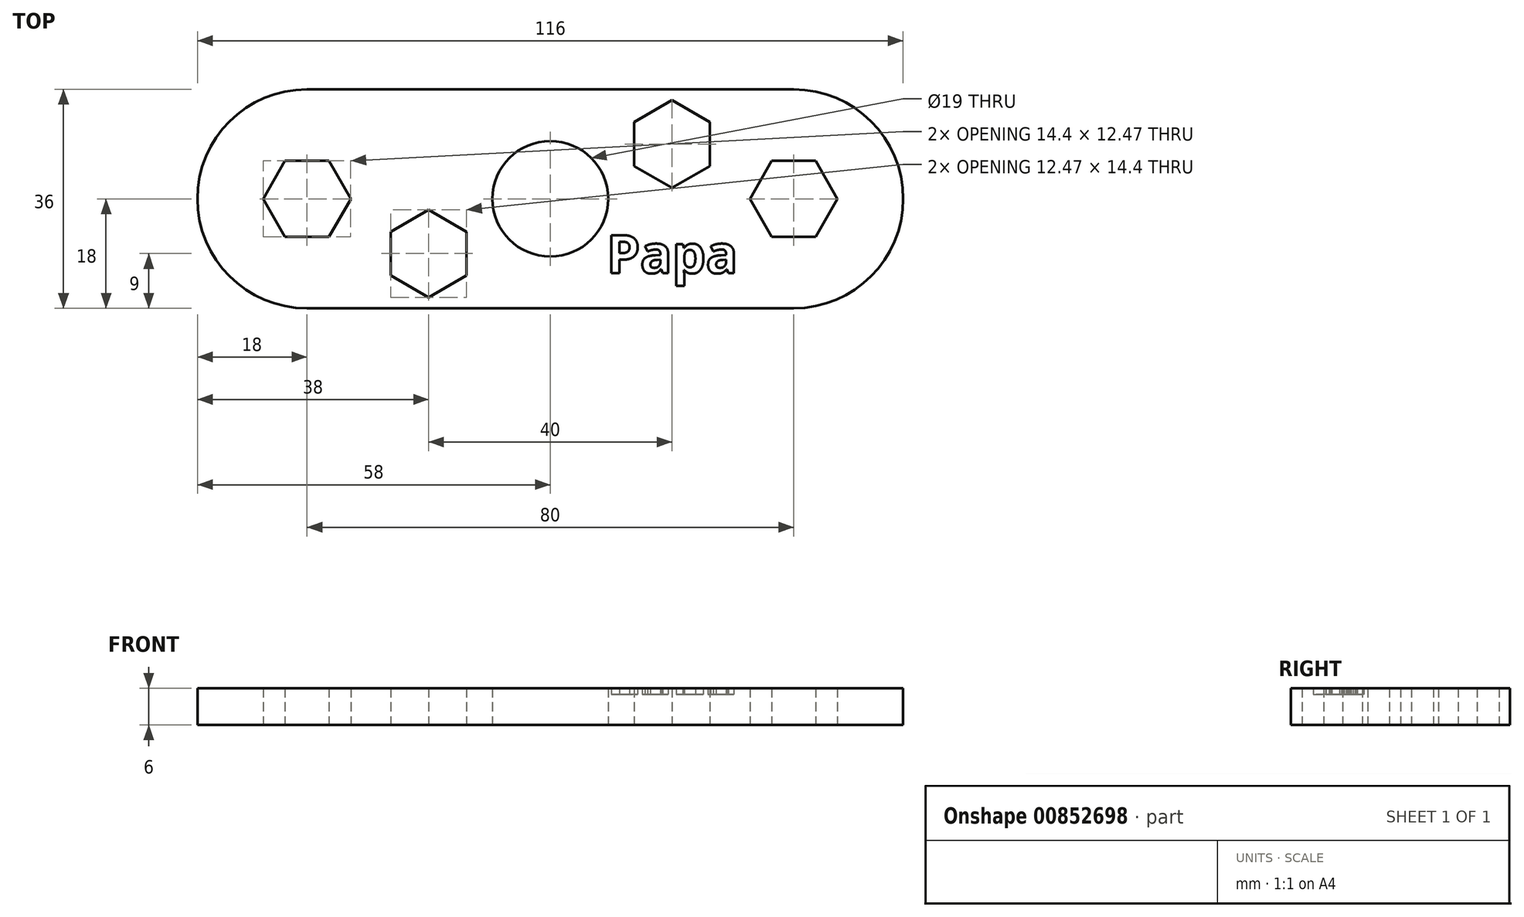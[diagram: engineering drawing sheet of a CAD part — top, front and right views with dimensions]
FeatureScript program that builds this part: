
annotation { "Feature Type Name" : "Feature", "Feature Type Description" : "" }
export const myFeature = defineFeature(function(context is Context, id is Id, definition is map)
    precondition{}
    {
        {
            var Q0;
            Q0=qCreatedBy(makeId("Top.planeOp"),FACE);
            var sketch = newSketch(context, id + "F0", { "sketchPlane" : qUnion([Q0])});
            skPoint(sketch, "E0.middle", {"position": v(0, 0) * mm});
            skCircle(sketch, "E1", {"center": v(0, 0) * mm, "radius": 9.5 * mm});
            skCircle(sketch, "E2.cCircle", {"center": v(40, 0) * mm, "radius": 7.2 * mm, "construction": true});
            skLineSegment(sketch, "E2.0", {"start": v(47.2, 0) * mm, "end": v(43.6, -6.24) * mm});
            skLineSegment(sketch, "E2.1", {"start": v(43.6, -6.24) * mm, "end": v(36.4, -6.24) * mm});
            skLineSegment(sketch, "E2.2", {"start": v(36.4, -6.24) * mm, "end": v(32.8, 0) * mm});
            skLineSegment(sketch, "E2.3", {"start": v(32.8, 0) * mm, "end": v(36.4, 6.24) * mm});
            skLineSegment(sketch, "E2.4", {"start": v(36.4, 6.24) * mm, "end": v(43.6, 6.24) * mm});
            skLineSegment(sketch, "E2.5", {"start": v(43.6, 6.24) * mm, "end": v(47.2, 0) * mm});
            skPoint(sketch, "E3", {"position": v(20, 0) * mm});
            skText(sketch, "E4", { "text": "Papa", "fontName": "OpenSans-Bold.ttf"});
            skLineSegment(sketch, "E5.top", {"start": v(0, 18) * mm, "end": v(40, 18) * mm});
            skLineSegment(sketch, "E6.top", {"start": v(40, 10) * mm, "end": v(40, 10) * mm});
            skLineSegment(sketch, "E7.top", {"start": v(0, 18) * mm, "end": v(-40, 18) * mm});
            skLineSegment(sketch, "E7.left", {"start": v(0, 0) * mm, "end": v(0, 18) * mm});
            skLineSegment(sketch, "E8.top", {"start": v(0, -18) * mm, "end": v(-40, -18) * mm});
            skLineSegment(sketch, "E8.left", {"start": v(0, 0) * mm, "end": v(0, -18) * mm});
            skLineSegment(sketch, "E9.top", {"start": v(0, -18) * mm, "end": v(40, -18) * mm});
            skArc(sketch, "E10", {"start": v(40, -18) * mm, "mid": v(58, 0) * mm, "end": v(40, 18) * mm});
            skArc(sketch, "E11", {"start": v(-40, 18) * mm, "mid": v(-58, 0) * mm, "end": v(-40, -18) * mm});
            skPoint(sketch, "E12", {"position": v(-20, -9) * mm});
            skCircle(sketch, "E13.cCircle", {"center": v(-20, -9) * mm, "radius": 7.2 * mm, "construction": true});
            skLineSegment(sketch, "E13.0", {"start": v(-20, -1.8) * mm, "end": v(-13.76, -5.4) * mm});
            skLineSegment(sketch, "E13.1", {"start": v(-13.76, -5.4) * mm, "end": v(-13.76, -12.6) * mm});
            skLineSegment(sketch, "E13.2", {"start": v(-13.76, -12.6) * mm, "end": v(-20, -16.2) * mm});
            skLineSegment(sketch, "E13.3", {"start": v(-20, -16.2) * mm, "end": v(-26.24, -12.6) * mm});
            skLineSegment(sketch, "E13.4", {"start": v(-26.24, -12.6) * mm, "end": v(-26.24, -5.4) * mm});
            skLineSegment(sketch, "E13.5", {"start": v(-26.24, -5.4) * mm, "end": v(-20, -1.8) * mm});
            skCircle(sketch, "E14.cCircle", {"center": v(-40, 0) * mm, "radius": 7.2 * mm, "construction": true});
            skLineSegment(sketch, "E14.0", {"start": v(-32.8, 0) * mm, "end": v(-36.4, -6.24) * mm});
            skLineSegment(sketch, "E14.1", {"start": v(-36.4, -6.24) * mm, "end": v(-43.6, -6.24) * mm});
            skLineSegment(sketch, "E14.2", {"start": v(-43.6, -6.24) * mm, "end": v(-47.2, 0) * mm});
            skLineSegment(sketch, "E14.3", {"start": v(-47.2, 0) * mm, "end": v(-43.6, 6.24) * mm});
            skLineSegment(sketch, "E14.4", {"start": v(-43.6, 6.24) * mm, "end": v(-36.4, 6.24) * mm});
            skLineSegment(sketch, "E14.5", {"start": v(-36.4, 6.24) * mm, "end": v(-32.8, 0) * mm});
            skPoint(sketch, "E15", {"position": v(20, 9) * mm});
            skCircle(sketch, "E16.cCircle", {"center": v(20, 9) * mm, "radius": 7.2 * mm, "construction": true});
            skLineSegment(sketch, "E16.0", {"start": v(20, 16.2) * mm, "end": v(26.24, 12.6) * mm});
            skLineSegment(sketch, "E16.1", {"start": v(26.24, 12.6) * mm, "end": v(26.24, 5.4) * mm});
            skLineSegment(sketch, "E16.2", {"start": v(26.24, 5.4) * mm, "end": v(20, 1.8) * mm});
            skLineSegment(sketch, "E16.3", {"start": v(20, 1.8) * mm, "end": v(13.76, 5.4) * mm});
            skLineSegment(sketch, "E16.4", {"start": v(13.76, 5.4) * mm, "end": v(13.76, 12.6) * mm});
            skLineSegment(sketch, "E16.5", {"start": v(13.76, 12.6) * mm, "end": v(20, 16.2) * mm});
            const initialGuessF0  = {"E4": [0.00927, -0.01223, 1, 0, 0.00629]};
            skSetInitialGuess(sketch, initialGuessF0);
            skSolve(sketch);
        }
        {
            var Q0;
            Q0 = qSketchRegion(id + "F0", true);
            extrude(context, id + "F1", {"entities" : qUnion([Q0]), "depth" : 6 * mm, "offsetDistance" : 25 * mm});
        }
        {
            var Q0;
            Q0=makeQuery(id+"F0.imprint","IMPRINT",FACE,{"disambiguationData":[TD([[makeQuery(id+"F0.imprint","IMPRINT",EDGE,{"derivedFrom":sQuery(id+"F0.wireOp",EDGE,"E4.sketch_text.stroke-0")}),-1.0]])]});
            var Q1;
            Q1=makeQuery(id+"F0.imprint","IMPRINT",FACE,{"disambiguationData":[TD([[makeQuery(id+"F0.imprint","IMPRINT",EDGE,{"derivedFrom":sQuery(id+"F0.wireOp",EDGE,"E4.sketch_text.stroke-16")}),-1.0]])]});
            var Q2;
            Q2=makeQuery(id+"F0.imprint","IMPRINT",FACE,{"disambiguationData":[TD([[makeQuery(id+"F0.imprint","IMPRINT",EDGE,{"derivedFrom":sQuery(id+"F0.wireOp",EDGE,"E4.sketch_text.stroke-41")}),-1.0]])]});
            var Q3;
            Q3=makeQuery(id+"F0.imprint","IMPRINT",FACE,{"disambiguationData":[TD([[makeQuery(id+"F0.imprint","IMPRINT",EDGE,{"derivedFrom":sQuery(id+"F0.wireOp",EDGE,"E4.sketch_text.stroke-64")}),-1.0]])]});
            extrude(context, id + "F2", {"entities" : qUnion([Q0, Q1, Q2, Q3]), "operationType" : NewBodyOperationType.ADD, "depth" : 5 * mm, "offsetDistance" : 25 * mm});
        }
        {
            var Q0;
            Q0=makeQuery(id+"F0.imprint","IMPRINT",FACE,{"disambiguationData":[TD([[makeQuery(id+"F0.imprint","IMPRINT",EDGE,{"derivedFrom":sQuery(id+"F0.wireOp",EDGE,"E4.sketch_text.stroke-82")}),1.0]])]});
            var Q1;
            Q1=makeQuery(id+"F0.imprint","IMPRINT",FACE,{"disambiguationData":[TD([[makeQuery(id+"F0.imprint","IMPRINT",EDGE,{"derivedFrom":sQuery(id+"F0.wireOp",EDGE,"E4.sketch_text.stroke-56")}),1.0]])]});
            var Q2;
            Q2=makeQuery(id+"F0.imprint","IMPRINT",FACE,{"disambiguationData":[TD([[makeQuery(id+"F0.imprint","IMPRINT",EDGE,{"derivedFrom":sQuery(id+"F0.wireOp",EDGE,"E4.sketch_text.stroke-34")}),1.0]])]});
            var Q3;
            Q3=makeQuery(id+"F0.imprint","IMPRINT",FACE,{"disambiguationData":[TD([[makeQuery(id+"F0.imprint","IMPRINT",EDGE,{"derivedFrom":sQuery(id+"F0.wireOp",EDGE,"E4.sketch_text.stroke-0")}),1.0]])]});
            extrude(context, id + "F3", {"entities" : qUnion([Q0, Q1, Q2, Q3]), "operationType" : NewBodyOperationType.ADD, "depth" : 6 * mm, "offsetDistance" : 25 * mm});
        }
    });
